# Revit family: Building-RicaricaVeicoliElettrici-GEWISS-JOINON-ION_PARETE
name_source: partatom
category: Apparecchi elettrici
units: mm (PartAtom-declared; Revit-internal decimal feet)

## family parameters
Condiviso = No
Host = Superficie
Mantenere orientamento annotazione = No
Punto di calcolo locali = No
Quota connettore circolare = Usa diametro
Taglio con vuoti quando caricato = No
Tipo di parte = Normale

## types (1)
- Building-RicaricaVeicoliElettrici-GEWISS-JOINON-ION_PARETE
    Attivazione ricarica = Gestito da remoto, via OCPP 1.6J
    Caratteristiche meccaniche = -
    Colore = Grigio, Testata RAL 7011
    Comunicazione = Kit Ethernet e Modem 4G con antenna di potenziamento
    Connettività: = LAN, WIFI, 4G
    Contatore di energia = SI (Tipo MID)
    Corrente erogata (max) = 32 A per socket (10 A per Tipo F)
    Corrente nominale: = 42 Ampere
    DC Leakage check = Attualmente non presente
    Descrizione = JOINON I-ON WALL CLOUD 22+22KW MID LAN+4G 1T2+1S
    Grado di protezione = IP54
    Human Interface = LED RGB e TFT Display
    IDF = 2f9b508c-7d31-4b7c-ae4d-7ca9aada2f83
    INPUT: = -
    Immagine tipo = ION_PARETE.jpg
    Lettore RFID = Si
    Materiale = Lamiera d'acciaio
    Modello = GWJ2123W
    Morsettiera: = 1 x (5 x 10 mm²) + 1 x (3 x 6 mm²)
    N. Prese Tipo 2 = 1 (+1 prese domestiche tipo F)
    Numero di prese (tipo) = 1 (Tipo 2 anti-vandalo,  con shutter) + 1 (Tipo F)
    OUTPUT : = -
    Personalizzabile: = SI (frontale)
    Potenza complessiva: = 25 Chilowatt
    Potenza di ricarica = 22 kW + 2,3 kW
    Potenza max. = 22 kW per socket (2,3 kW per Tipo F)
    Produttore = GEWISS S.p.A.
    Prospetto di default = 1219 mm
    Protezione magnetotermica = Attualmente non presente
    Protezioni = No
    Resistenza agli urti = IK10
    Riarmo protezioni da remoto = Attualmente non presente
    Simbolo in pianta = Sì
    Temperatura di utilizzo = -25 +50 °C
    Tensione nominale = 400 Volt
    Tensione nominale di isolamento (Ui) = 400 Volt
    Tipo di installazione e montaggio = A parete
    Tipo di protezione differenziale = Attualmente non presente
    Trattamento esterno = Anti-corrosione ed anti-graffito
    URL = https://www.gewiss.com
    Versione file RFA = 19.4
